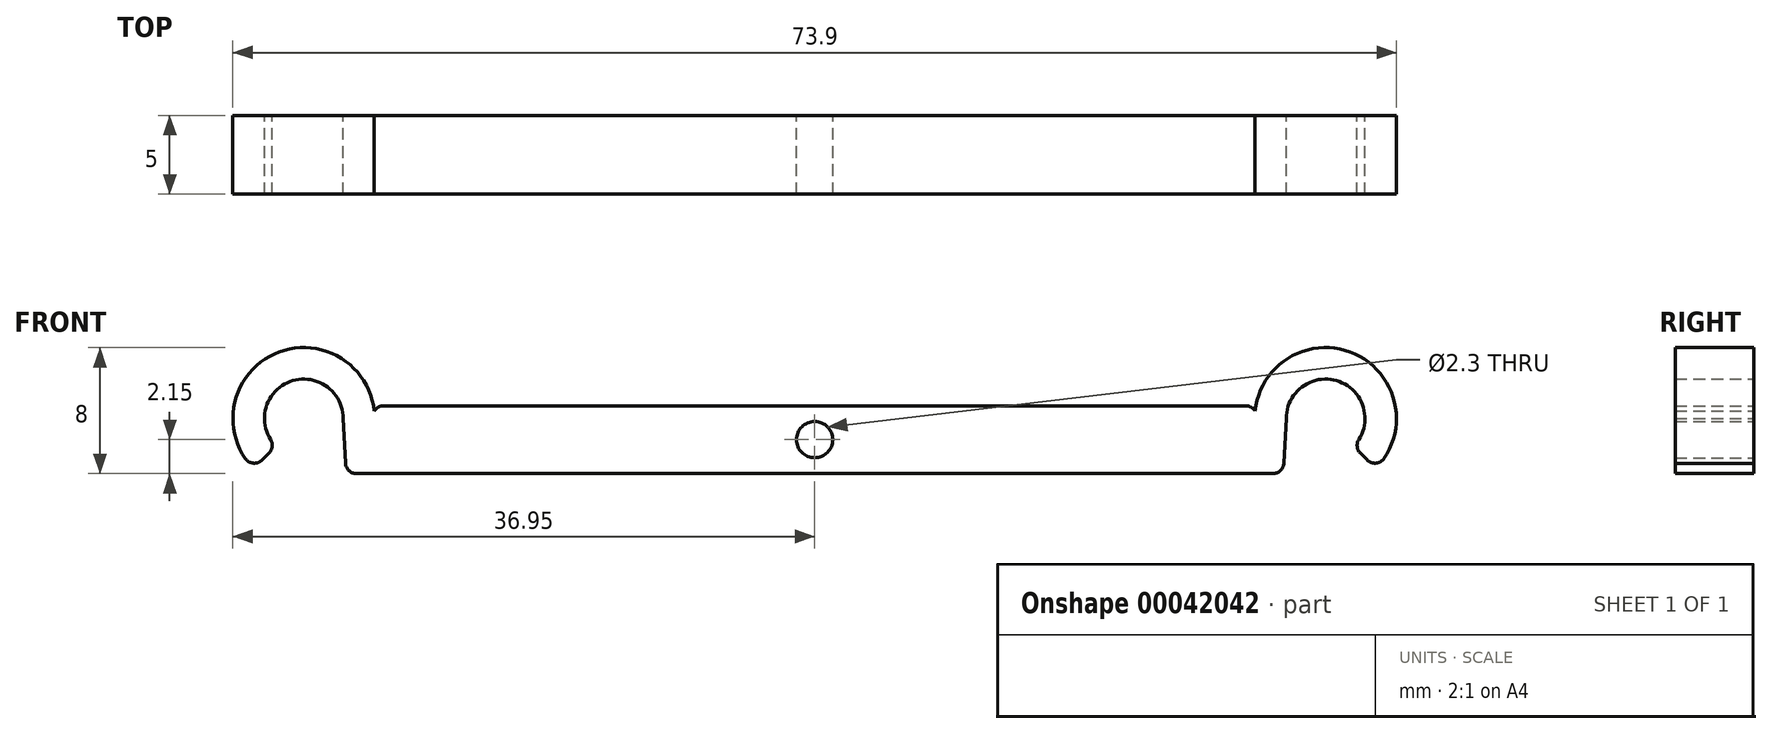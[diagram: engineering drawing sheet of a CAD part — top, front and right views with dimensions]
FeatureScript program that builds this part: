
annotation { "Feature Type Name" : "Feature", "Feature Type Description" : "" }
export const myFeature = defineFeature(function(context is Context, id is Id, definition is map)
    precondition{}
    {
        {
            var Q0;
            Q0=qCreatedBy(makeId("Front.planeOp"),FACE);
            var sketch = newSketch(context, id + "F0", { "sketchPlane" : qUnion([Q0])});
            skLineSegment(sketch, "E0", {"start": v(0, 0) * mm, "end": v(-28, 0) * mm});
            skLineSegment(sketch, "E1", {"start": v(-27.95, -0.8) * mm, "end": v(-28, 0) * mm});
            skArc(sketch, "E2", {"start": v(-27.95, -0.8) * mm, "mid": v(-34.17, 3.36) * mm, "end": v(-35.63, -3.98) * mm});
            skArc(sketch, "E3.0", {"start": v(-29.95, -0.8) * mm, "mid": v(-33.4, 1.5) * mm, "end": v(-34.22, -2.57) * mm});
            skLineSegment(sketch, "E4", {"start": v(-29.95, -0.8) * mm, "end": v(-29.95, -4.3) * mm, "construction": true});
            skLineSegment(sketch, "E5", {"start": v(-29.95, -4.3) * mm, "end": v(29.95, -4.3) * mm, "construction": true});
            skLineSegment(sketch, "E6", {"start": v(-27.95, -0.8) * mm, "end": v(-36.95, -0.8) * mm, "construction": true});
            skPoint(sketch, "E7", {"position": v(0, 0) * mm});
            skArc(sketch, "E8", {"start": v(0, -1) * mm, "mid": v(-1.15, -2.15) * mm, "end": v(0, -3.3) * mm});
            skLineSegment(sketch, "E9", {"start": v(0, 0) * mm, "end": v(0, -1) * mm});
            skPoint(sketch, "E10", {"position": v(0, -4.3) * mm});
            skPoint(sketch, "E11.orphan", {"position": v(-34.95, -0.8) * mm});
            skLineSegment(sketch, "E12", {"start": v(-35.63, -3.98) * mm, "end": v(-34.22, -2.57) * mm});
            skLineSegment(sketch, "E13", {"start": v(-29.95, -0.8) * mm, "end": v(-29.77, -4.3) * mm});
            skPoint(sketch, "E14.orphan", {"position": v(28, 0) * mm});
            skLineSegment(sketch, "E15", {"start": v(-29.77, -4.3) * mm, "end": v(0, -4.3) * mm});
            skLineSegment(sketch, "E16.trimOffspring", {"start": v(0, -3.3) * mm, "end": v(0, -4.3) * mm});
            skSolve(sketch);
        }
        {
            var Q0;
            Q0=qSketchRegion(id+"F0",true);
            extrude(context, id + "F1", {"entities" : qUnion([Q0]), "depth" : 5 * mm});
        }
        {
            var Q0;
            Q0=makeQuery(id+"F1.opExtrude","SWEPT_EDGE",EDGE,{"disambiguationData":[OSD([sQuery(id+"F0.wireOp",EDGE,"E0"),sQuery(id+"F0.wireOp",EDGE,"E1")])]});
            var Q1;
            Q1=makeQuery(id+"F1.opExtrude","SWEPT_EDGE",EDGE,{"disambiguationData":[OSD([sQuery(id+"F0.wireOp",EDGE,"E13"),sQuery(id+"F0.wireOp",EDGE,"E15")])]});
            var Q2;
            Q2=makeQuery(id+"F1.opExtrude","SWEPT_EDGE",EDGE,{"disambiguationData":[OSD([sQuery(id+"F0.wireOp",EDGE,"E3.0"),sQuery(id+"F0.wireOp",EDGE,"E12")])]});
            var Q3;
            Q3=makeQuery(id+"F1.opExtrude","SWEPT_EDGE",EDGE,{"disambiguationData":[OSD([sQuery(id+"F0.wireOp",EDGE,"E2"),sQuery(id+"F0.wireOp",EDGE,"E12")])]});
            fillet(context, id + "F2", {"entities" : qUnion([Q0, Q1, Q2, Q3]), "radius" : .7 * mm, "tangentPropagation" : true, "allowEdgeOverflow" : false});
        }
        {
            var Q0;
            Q0=makeQuery(id+"F1.opExtrude","SWEPT_BODY",BODY,{"disambiguationData":[OSD([sQuery(id+"F0.wireOp",EDGE,"E0"),sQuery(id+"F0.wireOp",EDGE,"E1"),sQuery(id+"F0.wireOp",EDGE,"E2"),sQuery(id+"F0.wireOp",EDGE,"E3.0"),sQuery(id+"F0.wireOp",EDGE,"E8"),sQuery(id+"F0.wireOp",EDGE,"E9"),sQuery(id+"F0.wireOp",EDGE,"E12"),sQuery(id+"F0.wireOp",EDGE,"E13"),sQuery(id+"F0.wireOp",EDGE,"E15"),sQuery(id+"F0.wireOp",EDGE,"E16.trimOffspring")])]});
            var Q1;
            Q1=qCreatedBy(makeId("Right.planeOp"),FACE);
            mirror(context, id + "F3", {"operationType" : NewBodyOperationType.ADD, "entities" : qUnion([Q0]), "mirrorPlane" : qUnion([Q1])});
        }
    });
